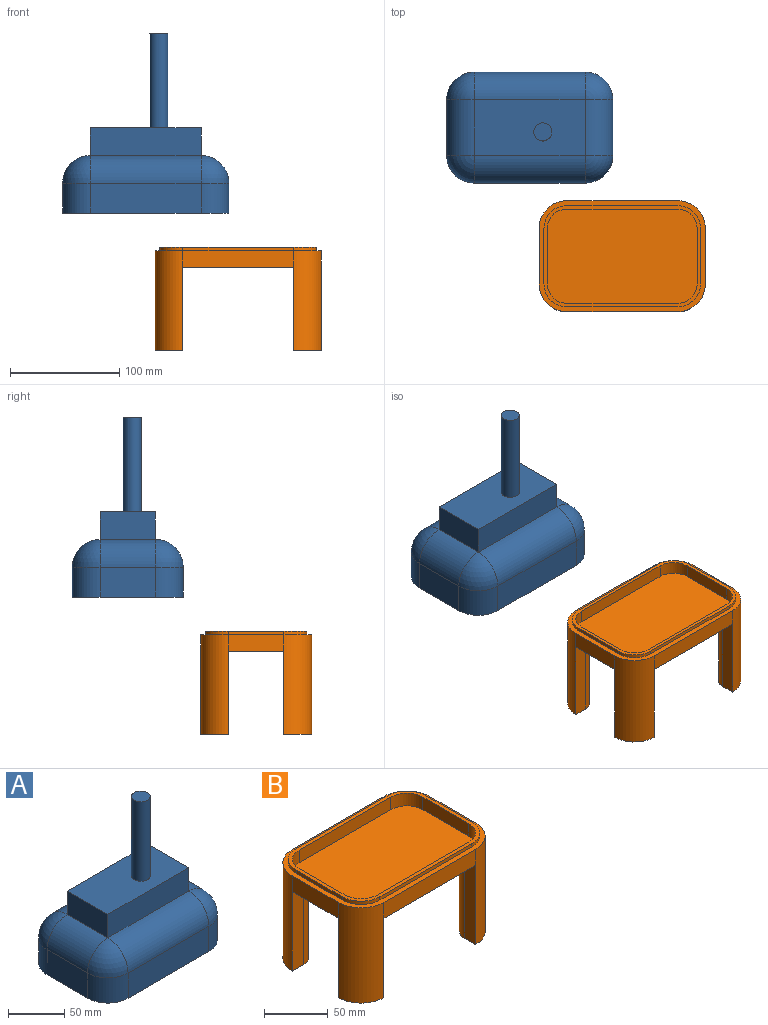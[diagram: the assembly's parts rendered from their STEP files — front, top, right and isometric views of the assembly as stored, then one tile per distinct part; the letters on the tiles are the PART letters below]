
ASSEMBLY  parts=2 mates=2
PART A: 41 faces, bbox 152.4x101.6x164.6 mm
  f0: plane 152.4x101.6mm, normal (0,0,-1), area 1386.3mm2, adj f1,f2,f3,f4,f5,f7,f10,f16
  f1: plane 50.8x27.43mm, normal (-1,0,0), area 1393.5mm2, adj f0,f7,f13,f16
  f2: plane 101.6x27.43mm, normal (0,-1,0), area 2787.1mm2, adj f0,f10,f14,f16
  f3: plane 50.8x27.43mm, normal (1,0,0), area 1393.5mm2, adj f0,f5,f9,f10
  f4: plane 101.6x27.43mm, normal (0,1,0), area 2787.1mm2, adj f0,f5,f7,f8
  f5: cylinder r=25.4mm len=27.43mm, axis (0,0,1), area 1094.5mm2, adj f0,f3,f4,f6
  f6: sphere r=25.4mm, area 1013.4mm2, adj f5,f8,f9
  f7: cylinder r=25.4mm len=27.43mm, axis (0,0,-1), area 1094.5mm2, adj f0,f1,f4,f11
  f8: cylinder r=25.4mm len=101.6mm, axis (1,0,0), area 4053.7mm2, adj f4,f6,f11,f37
  f9: cylinder r=25.4mm len=50.8mm, axis (0,-1,0), area 2026.8mm2, adj f3,f6,f12,f36
  f10: cylinder r=25.4mm len=27.43mm, axis (0,0,-1), area 1094.5mm2, adj f0,f2,f3,f12
  f11: sphere r=25.4mm, area 1013.4mm2, adj f7,f8,f13
  f12: sphere r=25.4mm, area 1013.4mm2, adj f9,f10,f14
  f13: cylinder r=25.4mm len=50.8mm, axis (0,1,0), area 2026.8mm2, adj f1,f11,f15,f34
  f14: cylinder r=25.4mm len=101.6mm, axis (-1,0,0), area 4053.7mm2, adj f2,f12,f15,f35
  f15: sphere r=25.4mm, area 1013.4mm2, adj f13,f14,f16
  f16: cylinder r=25.4mm len=27.43mm, axis (0,0,1), area 1094.5mm2, adj f0,f1,f2,f15
  f17: plane 50.8x27.43mm, normal (1,0,0), area 1393.5mm2, adj f0,f24,f30,f33
  f18: plane 101.6x27.43mm, normal (0,1,0), area 2787.1mm2, adj f0,f27,f31,f33
  f19: plane 50.8x27.43mm, normal (-1,0,0), area 1393.5mm2, adj f0,f22,f26,f27
  f20: plane 101.6x27.43mm, normal (0,-1,0), area 2787.1mm2, adj f0,f22,f24,f25
  f21: plane 101.6x50.8mm, normal (0,0,-1), area 5161.3mm2, adj f25,f26,f30,f31
  f22: cylinder r=22.35mm len=27.43mm, axis (0,0,1), area 963.1mm2, adj f0,f19,f20,f23
  f23: sphere r=22.35mm, area 784.8mm2, adj f22,f25,f26
  f24: cylinder r=22.35mm len=27.43mm, axis (0,0,-1), area 963.1mm2, adj f0,f17,f20,f28
  f25: cylinder r=22.35mm len=101.6mm, axis (1,0,0), area 3567.2mm2, adj f20,f21,f23,f28
  f26: cylinder r=22.35mm len=50.8mm, axis (0,-1,0), area 1783.6mm2, adj f19,f21,f23,f29
  f27: cylinder r=22.35mm len=27.43mm, axis (0,0,-1), area 963.1mm2, adj f0,f18,f19,f29
  f28: sphere r=22.35mm, area 784.8mm2, adj f24,f25,f30
  f29: sphere r=22.35mm, area 784.8mm2, adj f26,f27,f31
  f30: cylinder r=22.35mm len=50.8mm, axis (0,1,0), area 1783.6mm2, adj f17,f21,f28,f32
  f31: cylinder r=22.35mm len=101.6mm, axis (-1,0,0), area 3567.2mm2, adj f18,f21,f29,f32
  f32: sphere r=22.35mm, area 784.8mm2, adj f30,f31,f33
  f33: cylinder r=22.35mm len=27.43mm, axis (0,0,1), area 963.1mm2, adj f0,f17,f18,f32
  f34: plane 50.8x25.4mm, normal (-1,0,0), area 1290.3mm2, adj f13,f35,f37,f38
  f35: plane 101.6x25.4mm, normal (0,-1,0), area 2580.6mm2, adj f14,f34,f36,f38
  f36: plane 50.8x25.4mm, normal (1,0,0), area 1290.3mm2, adj f9,f35,f37,f38
  f37: plane 101.6x25.4mm, normal (0,1,0), area 2580.6mm2, adj f8,f34,f36,f38
  f38: plane 101.6x50.8mm, normal (0,0,1), area 4945.3mm2, adj f34,f35,f36,f37,f39
  f39: cylinder r=8.29mm len=86.33mm, axis (0,0,-1), area 4497.2mm2, adj f38,f40
  f40: plane 16.58x16.58mm, normal (0,0,1), area 216mm2, adj f39
PART B: 44 faces, bbox 152.4x101.6x94.6 mm
  f0: plane 25.4x25.4mm, normal (0,0,-1), area 472.1mm2, adj f11,f17,f18,f25
  f1: plane 25.4x25.4mm, normal (0,0,-1), area 472.1mm2, adj f12,f15,f21,f23
  f2: plane 76.2x12.7mm, normal (-1,0,0), area 967.7mm2, adj f13,f14,f16,f22
  f3: plane 76.2x12.7mm, normal (1,0,0), area 967.7mm2, adj f5,f10,f16,f24
  f4: plane 101.6x15.24mm, normal (0,-1,0), area 1548.4mm2, adj f9,f11,f12,f16
  f5: plane 25.4x25.4mm, normal (0,0,-1), area 472.1mm2, adj f3,f10,f19,f24
  f6: plane 101.6x15.24mm, normal (0,1,0), area 1548.4mm2, adj f9,f10,f13,f16
  f7: plane 50.8x15.24mm, normal (-1,0,0), area 774.2mm2, adj f9,f10,f11,f16
  f8: plane 50.8x15.24mm, normal (1,0,0), area 774.2mm2, adj f9,f12,f13,f16
  f9: plane 152.4x101.6mm, normal (0,0,1), area 2002.2mm2, adj f4,f6,f7,f8,f10,f11,f12,f13
  f10: cylinder r=25.4mm len=91.44mm, axis (0,0,1), area 3648.3mm2, adj f3,f5,f6,f7,f9,f19
  f11: cylinder r=25.4mm len=91.44mm, axis (0,0,-1), area 3648.3mm2, adj f0,f4,f7,f9,f17,f18
  f12: cylinder r=25.4mm len=91.44mm, axis (0,0,1), area 3648.3mm2, adj f1,f4,f8,f9,f15,f21
  f13: cylinder r=25.4mm len=91.44mm, axis (0,0,-1), area 3648.3mm2, adj f2,f6,f8,f9,f14,f20
  f14: plane 25.4x25.4mm, normal (0,0,-1), area 472.1mm2, adj f2,f13,f20,f22
  f15: plane 76.2x12.7mm, normal (-1,0,0), area 967.7mm2, adj f1,f12,f16,f23
  f16: plane 152.4x101.6mm, normal (0,0,-1), area 13041.7mm2, adj f2,f3,f4,f6,f7,f8,f15,f17
  f17: plane 76.2x12.7mm, normal (1,0,0), area 967.7mm2, adj f0,f11,f16,f25
  f18: plane 76.2x12.7mm, normal (0,1,0), area 967.7mm2, adj f0,f11,f16,f25
  f19: plane 76.2x12.7mm, normal (0,-1,0), area 967.7mm2, adj f5,f10,f16,f24
  f20: plane 76.2x12.7mm, normal (0,-1,0), area 967.7mm2, adj f13,f14,f16,f22
  f21: plane 76.2x12.7mm, normal (0,1,0), area 967.7mm2, adj f1,f12,f16,f23
  f22: cylinder r=12.7mm len=76.2mm, axis (0,0,1), area 1520.1mm2, adj f2,f14,f16,f20
  f23: cylinder r=12.7mm len=76.2mm, axis (0,0,-1), area 1520.1mm2, adj f1,f15,f16,f21
  f24: cylinder r=12.7mm len=76.2mm, axis (0,0,-1), area 1520.1mm2, adj f3,f5,f16,f19
  f25: cylinder r=12.7mm len=76.2mm, axis (0,0,1), area 1520.1mm2, adj f0,f16,f17,f18
  f26: plane 101.6x3.18mm, normal (0,1,0), area 322.6mm2, adj f9,f27,f33,f34
  f27: cylinder r=20.96mm len=20.96mm, axis (0,0,-1), area 104.5mm2, adj f9,f26,f28,f34
  f28: plane 50.8x3.18mm, normal (-1,0,0), area 161.3mm2, adj f9,f27,f29,f34
  f29: cylinder r=20.96mm len=20.96mm, axis (0,0,-1), area 104.5mm2, adj f9,f28,f30,f34
  f30: plane 101.6x3.18mm, normal (0,-1,0), area 322.6mm2, adj f9,f29,f31,f34
  f31: cylinder r=20.96mm len=20.96mm, axis (0,0,-1), area 104.5mm2, adj f9,f30,f32,f34
  f32: plane 50.8x3.18mm, normal (1,0,0), area 161.3mm2, adj f9,f31,f33,f34
  f33: cylinder r=20.96mm len=20.96mm, axis (0,0,-1), area 104.5mm2, adj f9,f26,f32,f34
  f34: plane 143.51x92.71mm, normal (0,0,1), area 1354.1mm2, adj f26,f27,f28,f29,f30,f31,f32,f33
  f35: plane 137.16x86.36mm, normal (0,0,1), area 11573.8mm2, adj f36,f37,f38,f39,f40,f41,f42,f43
  f36: cylinder r=17.78mm len=17.78mm, axis (0,0,1), area 337mm2, adj f34,f35,f37,f43
  f37: plane 50.8x12.07mm, normal (1,0,0), area 612.9mm2, adj f34,f35,f36,f38
  f38: cylinder r=17.78mm len=17.78mm, axis (0,0,1), area 337mm2, adj f34,f35,f37,f39
  f39: plane 101.6x12.07mm, normal (0,1,0), area 1225.8mm2, adj f34,f35,f38,f40
  f40: cylinder r=17.78mm len=17.78mm, axis (0,0,1), area 337mm2, adj f34,f35,f39,f41
  f41: plane 50.8x12.07mm, normal (-1,0,0), area 612.9mm2, adj f34,f35,f40,f42
  f42: cylinder r=17.78mm len=17.78mm, axis (0,0,1), area 337mm2, adj f34,f35,f41,f43
  f43: plane 101.6x12.07mm, normal (0,-1,0), area 1225.8mm2, adj f34,f35,f36,f42
PLACE A t=(-203.18,107.85,54.68)mm
PLACE B t=(-65.31,13.67,5.13)mm
MATE parallel B.f4 <-> A.f2  axis (0,-1,0) through (-105.71,-56.57,12.75)mm
MATE parallel B.f9 <-> A.f0  axis (0,0,1) through (-105.71,-5.77,20.37)mm
